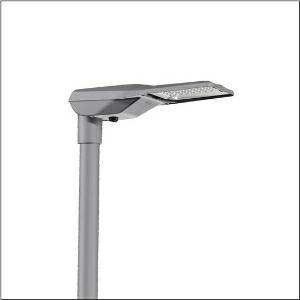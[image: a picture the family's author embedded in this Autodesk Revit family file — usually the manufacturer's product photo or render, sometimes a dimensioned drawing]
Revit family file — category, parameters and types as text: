
# Revit family: streetlight_sl_21_mini___st1_0a_5xe2d33r08hb_bda5
name_source: partatom
category: Lighting Fixtures
units: mm (PartAtom-declared; Revit-internal decimal feet)

## family parameters
Cut with Voids When Loaded = No
Host = Face
Light Source = No
Part Type = Normal
Room Calculation Point = No
Round Connector Dimension = Use Diameter
Shared = No

## types (1)
- --- (1 x LED, 9040 lm, 66 W, 3000K)
    Apparent Load = 66 VA
    CIE Flux Codes = 37 72 97 100 100
    Color Rendering = 70
    Color Temperature = 3000K
    Default Elevation = 1800 mm
    Description = Streetlight SL 21 mini, mast luminaire, primary light control with lens, of PMMA, primary optical cover: cover, of toughened safety glass, transparent, light distribution: ST1.0a, light emission: direct distribution, primary light characteristic: asymmetric, installation type: side-entry, post-top, LED, High Power LED, rated luminous flux: 9.040lm, luminous efficacy: 137lm/W, light colour: 730, colour temperature: 3000K, control gear: D4i, control: flexible luminous flux parameterisation, time-dependent luminous flux control, constant luminous flux control, overheat protection, pre-setting: logarithmic dimming characteristic, mains connection: 220..240V, AC, 50/60Hz, start of lifetime: 66W, end of service life: 69W, reduction: 30W, luminaire housing, of diecast aluminium, powder-coated, Siteco® metallic grey (DB 702S), corrosivity category C5 mid according to DIN EN ISO 12944, please order mast flange separately, inclination adjustable: 0°, 5°, 10°, 15°, sealing non-destructively replaceable, multi-level sealing system, length: 628mm, width: 235mm, height: 110mm, mast flange for spigot size: 42mm (side-entry): 5XC10008XM4, 60/48mm (side-entry/post-top): 5XC10108XM2, 76/60mm (side-entry/post-top): 5XC10108XM1, mounting height: 4..8m, Smart Interface below, protection rating (complete): IP66, insulation class (complete): insulation class II (safety insulation), certification: CE, ENEC, ENEC+, VDE, impact resistance: IK10, permissible operating ambient temperature for outdoor applications: -40..+50°C, standard-compliant lighting for roads and squares, packaging unit: 1 piece

Light Distribution: ST1.0a
    Height = 110 mm
    Lamp = 1 x LED
    Lamp Light Flux = 9040 lm
    Lamp Power = 66 W
    Lamp count = 1
    Length = 625 mm
    Luminous efficacy = 137 lm/W
    Manufacturer = Siteco
    ModVariant = No
    Model = 5XE2D33R08HB
    Number of Poles = 1
    OnlyDefault = Yes
    Power Factor = 1
    Product Name = Streetlight SL 21 mini | ST1.0a
    Product group = mast luminaire | pylon top
    ProductGroupID = 6100
    Protection Class = Protection class II
    Protection Degree = IP 66
    RLX_Detail_Level = 1
    RLX_Emergency_Light_Flux = 0 lm
    RLX_Emergency_Type = 0
    RLX_Emergency_Type_DB = No
    RlxData = <blob elided: 26261 chars, md5=c760a32a>
    Socket = socket
    Standby Power = 0 W
    System Light Flux = 9040 lm
    System Power = 66 W
    Type Comments = factory setting: luminous flux: 100 % | dim-lin: 254 | 670 mA
    Type Image = l_1003516.jpg
    URL = http://relux.com
    VarID = @adj_210067
    Voltage = 0 V
    Weight = 0.00 kg
    Width = 234 mm

## geometry (parser evidence)
native form markers: Blend x4, Sweep x10
no freeform markers — native parametric forms only
